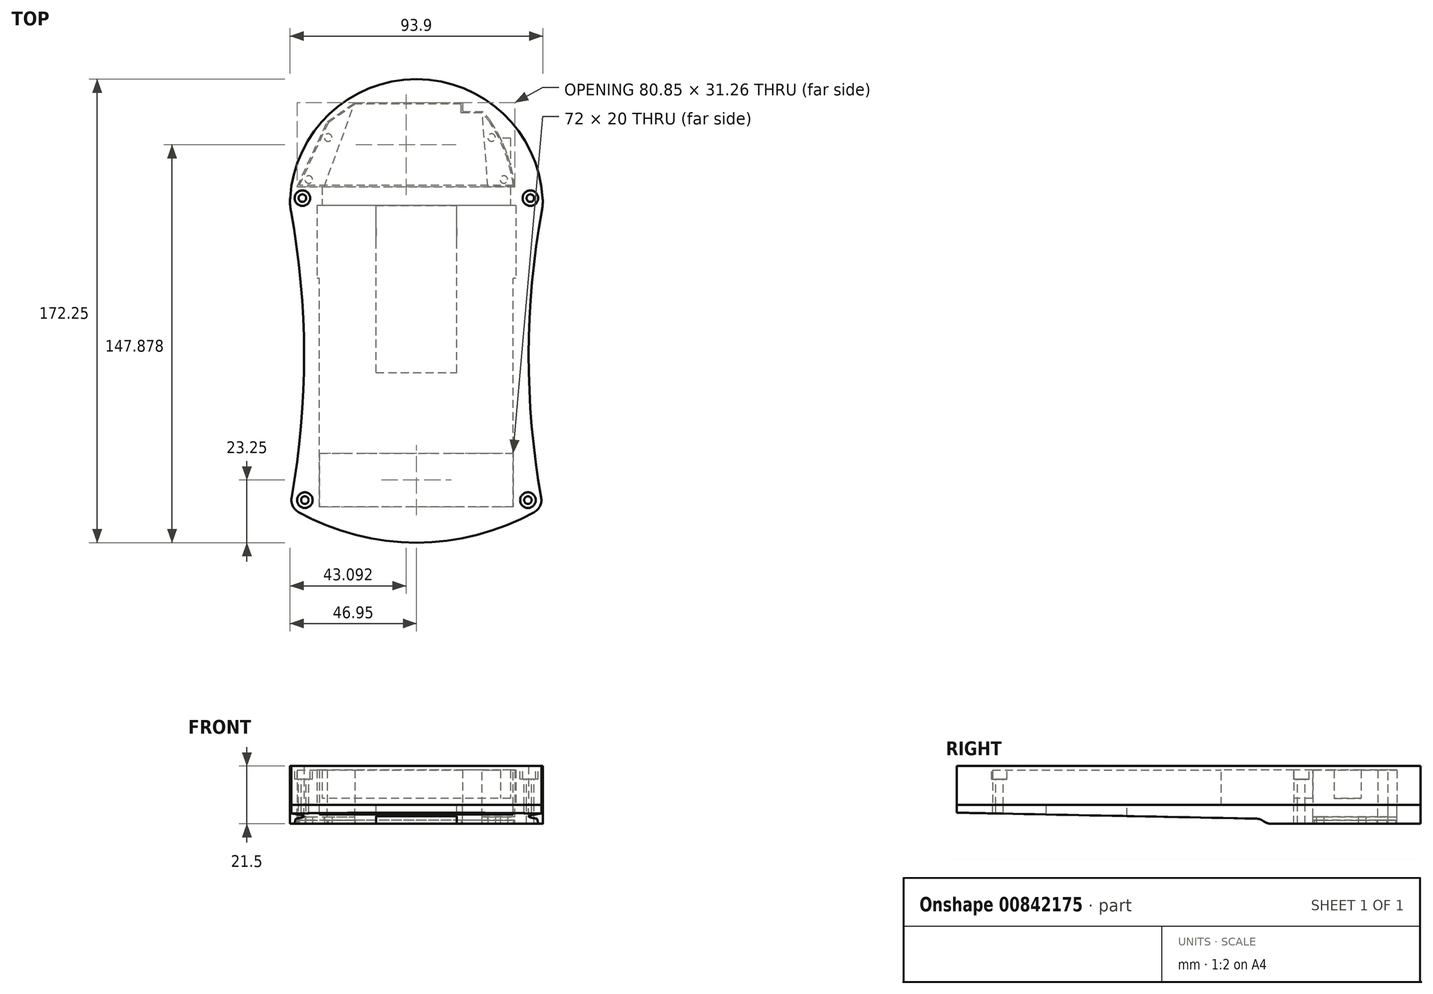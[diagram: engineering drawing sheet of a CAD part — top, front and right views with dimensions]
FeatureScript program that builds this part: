
annotation { "Feature Type Name" : "Feature", "Feature Type Description" : "" }
export const myFeature = defineFeature(function(context is Context, id is Id, definition is map)
    precondition{}
    {
        {
            var Q0;
            Q0=qCreatedBy(makeId("Top.planeOp"),FACE);
            var sketch = newSketch(context, id + "F0", { "sketchPlane" : qUnion([Q0])});
            skLineSegment(sketch, "E0.bottom", {"start": v(36, -56) * mm, "end": v(-36, -56) * mm});
            skLineSegment(sketch, "E0.top", {"start": v(36, 56) * mm, "end": v(-36, 56) * mm});
            skLineSegment(sketch, "E0.left", {"start": v(36, -56) * mm, "end": v(36, 56) * mm});
            skLineSegment(sketch, "E0.right", {"start": v(-36, -56) * mm, "end": v(-36, 56) * mm});
            skPoint(sketch, "E0.middle", {"position": v(0, 0) * mm});
            skArc(sketch, "E1", {"start": v(47, 56) * mm, "mid": v(0, 103) * mm, "end": v(-47, 56) * mm});
            skArc(sketch, "E2", {"start": v(-47, -56) * mm, "mid": v(-41.73, 0) * mm, "end": v(-47, 56) * mm});
            skLineSegment(sketch, "E3", {"start": v(0, 117.63) * mm, "end": v(0, -101.58) * mm, "construction": true});
            skLineSegment(sketch, "E4", {"start": v(-114.42, 0) * mm, "end": v(113.04, 0) * mm, "construction": true});
            skArc(sketch, "E5.MirrorCS", {"start": v(47, -56) * mm, "mid": v(0, -103) * mm, "end": v(-47, -56) * mm});
            skArc(sketch, "E6.MirrorCS", {"start": v(47, -56) * mm, "mid": v(41.73, 0) * mm, "end": v(47, 56) * mm});
            skSolve(sketch);
        }
        {
            var Q0;
            Q0=makeQuery(id+"F0.imprint","IMPRINT",FACE,{"disambiguationData":[TD([[makeQuery(id+"F0.imprint","IMPRINT",EDGE,{"derivedFrom":sQuery(id+"F0.wireOp",EDGE,"E0.bottom")}),1.0]])]});
            extrude(context, id + "F1", {"entities" : qUnion([Q0]), "depth" : 14.5 * mm, "offsetDistance" : 25 * mm});
        }
        {
            var Q0;
            Q0=makeQuery(id+"F1.opExtrude","CAP_FACE",FACE,{"disambiguationData":[OSD([sQuery(id+"F0.wireOp",EDGE,"E0.bottom"),sQuery(id+"F0.wireOp",EDGE,"E0.top"),sQuery(id+"F0.wireOp",EDGE,"E0.left"),sQuery(id+"F0.wireOp",EDGE,"E0.right"),sQuery(id+"F0.wireOp",EDGE,"E1"),sQuery(id+"F0.wireOp",EDGE,"E2"),sQuery(id+"F0.wireOp",EDGE,"E5.MirrorCS"),sQuery(id+"F0.wireOp",EDGE,"E6.MirrorCS")])],"isStart":false});
            var sketch = newSketch(context, id + "F2", { "sketchPlane" : qUnion([Q0])});
            skLineSegment(sketch, "E7.bottom", {"start": v(36, -56) * mm, "end": v(-36, -56) * mm});
            skLineSegment(sketch, "E7.top", {"start": v(36, 56) * mm, "end": v(-36, 56) * mm});
            skLineSegment(sketch, "E7.left", {"start": v(36, -56) * mm, "end": v(36, 56) * mm});
            skLineSegment(sketch, "E7.right", {"start": v(-36, -56) * mm, "end": v(-36, 56) * mm});
            skPoint(sketch, "E7.middle", {"position": v(0, 0) * mm});
            skSolve(sketch);
        }
        {
            var Q0;
            Q0=qSketchRegion(id+"F2",true);
            extrude(context, id + "F3", {"entities" : qUnion([Q0]), "operationType" : NewBodyOperationType.ADD, "oppositeDirection" : true, "depth" : 1.5 * mm, "offsetDistance" : 25 * mm});
        }
        {
            var Q0;
            Q0=makeQuery(id+"F1.opExtrude","CAP_FACE",FACE,{"disambiguationData":[OSD([sQuery(id+"F0.wireOp",EDGE,"E0.bottom"),sQuery(id+"F0.wireOp",EDGE,"E0.top"),sQuery(id+"F0.wireOp",EDGE,"E0.left"),sQuery(id+"F0.wireOp",EDGE,"E0.right"),sQuery(id+"F0.wireOp",EDGE,"E1"),sQuery(id+"F0.wireOp",EDGE,"E2"),sQuery(id+"F0.wireOp",EDGE,"E5.MirrorCS"),sQuery(id+"F0.wireOp",EDGE,"E6.MirrorCS")])],"isStart":true});
            var sketch = newSketch(context, id + "F4", { "sketchPlane" : qUnion([Q0])});
            skLineSegment(sketch, "E8", {"start": v(0, -56) * mm, "end": v(0, -29) * mm, "construction": true});
            skLineSegment(sketch, "E9.bottom", {"start": v(37, -56) * mm, "end": v(-37, -56) * mm});
            skLineSegment(sketch, "E9.top", {"start": v(37, -29) * mm, "end": v(-37, -29) * mm});
            skLineSegment(sketch, "E9.left", {"start": v(37, -56) * mm, "end": v(37, -29) * mm});
            skLineSegment(sketch, "E9.right", {"start": v(-37, -56) * mm, "end": v(-37, -29) * mm});
            skPoint(sketch, "E9.middle", {"position": v(0, -42.5) * mm});
            skSolve(sketch);
        }
        {
            var Q0;
            Q0=qSketchRegion(id+"F4",true);
            var Q1;
            Q1=makeQuery(id+"F3.opExtrude","CAP_FACE",FACE,{"disambiguationData":[OSD([sQuery(id+"F2.wireOp",EDGE,"E7.bottom"),sQuery(id+"F2.wireOp",EDGE,"E7.top"),sQuery(id+"F2.wireOp",EDGE,"E7.left"),sQuery(id+"F2.wireOp",EDGE,"E7.right")])],"isStart":false});
            extrude(context, id + "F5", {"entities" : qUnion([Q0]), "operationType" : NewBodyOperationType.REMOVE, "endBound" : BoundingType.UP_TO_SURFACE, "oppositeDirection" : true, "depth" : 25 * mm, "endBoundEntityFace" : qUnion([Q1]), "offsetDistance" : 25 * mm});
        }
        {
            var Q0;
            Q0=makeQuery(id+"F1.opExtrude","CAP_FACE",FACE,{"disambiguationData":[OSD([sQuery(id+"F0.wireOp",EDGE,"E0.bottom"),sQuery(id+"F0.wireOp",EDGE,"E0.top"),sQuery(id+"F0.wireOp",EDGE,"E0.left"),sQuery(id+"F0.wireOp",EDGE,"E0.right"),sQuery(id+"F0.wireOp",EDGE,"E1"),sQuery(id+"F0.wireOp",EDGE,"E2"),sQuery(id+"F0.wireOp",EDGE,"E5.MirrorCS"),sQuery(id+"F0.wireOp",EDGE,"E6.MirrorCS")])],"isStart":true});
            var sketch = newSketch(context, id + "F6", { "sketchPlane" : qUnion([Q0])});
            skArc(sketch, "E10", {"start": v(47, 56) * mm, "mid": v(0, 69.25) * mm, "end": v(-47, 56) * mm});
            skArc(sketch, "E11.0", {"start": v(47, 56) * mm, "mid": v(0, 103) * mm, "end": v(-47, 56) * mm});
            skSolve(sketch);
        }
        {
            var Q0;
            Q0=qSketchRegion(id+"F6",true);
            extrude(context, id + "F7", {"entities" : qUnion([Q0]), "operationType" : NewBodyOperationType.REMOVE, "oppositeDirection" : true, "depth" : 25 * mm, "offsetDistance" : 25 * mm});
        }
        {
            var Q0;
            Q0=makeQuery(id+"F1.opExtrude","CAP_FACE",FACE,{"disambiguationData":[OSD([sQuery(id+"F0.wireOp",EDGE,"E0.bottom"),sQuery(id+"F0.wireOp",EDGE,"E0.top"),sQuery(id+"F0.wireOp",EDGE,"E0.left"),sQuery(id+"F0.wireOp",EDGE,"E0.right"),sQuery(id+"F0.wireOp",EDGE,"E1"),sQuery(id+"F0.wireOp",EDGE,"E2"),sQuery(id+"F0.wireOp",EDGE,"E5.MirrorCS"),sQuery(id+"F0.wireOp",EDGE,"E6.MirrorCS")])],"isStart":true});
            var sketch = newSketch(context, id + "F8", { "sketchPlane" : qUnion([Q0])});
            skArc(sketch, "E12", {"start": v(27.76, -87.12) * mm, "mid": v(33.54, -75.56) * mm, "end": v(36.57, -63) * mm});
            skLineSegment(sketch, "E13", {"start": v(0, 109.51) * mm, "end": v(0, -146.95) * mm, "construction": true});
            skArc(sketch, "E14.MirrorCS", {"start": v(-27.76, -87.12) * mm, "mid": v(-33.54, -75.56) * mm, "end": v(-36.57, -63) * mm});
            skLineSegment(sketch, "E15", {"start": v(-36.57, -63) * mm, "end": v(36.57, -63) * mm});
            skPoint(sketch, "E16.orphan", {"position": v(-47, -56) * mm});
            skPoint(sketch, "E17.orphan", {"position": v(47, -56) * mm});
            skPoint(sketch, "E18.orphan", {"position": v(37, -56) * mm});
            skPoint(sketch, "E19.orphan", {"position": v(-37, -56) * mm});
            skArc(sketch, "E20.0", {"start": v(20.57, -93.76) * mm, "mid": v(0, -99) * mm, "end": v(-20.57, -93.76) * mm});
            skPoint(sketch, "E21.orphan", {"position": v(-16, -100.2) * mm});
            skPoint(sketch, "E22.orphan", {"position": v(16, -100.2) * mm});
            skPoint(sketch, "E23.visualSharp", {"position": v(-25, -90.99) * mm});
            skArc(sketch, "E23.filletArc", {"start": v(-27.76, -87.12) * mm, "mid": v(-24.57, -90.89) * mm, "end": v(-20.57, -93.76) * mm});
            skPoint(sketch, "E24.visualSharp", {"position": v(25, -90.99) * mm});
            skArc(sketch, "E24.filletArc", {"start": v(20.57, -93.76) * mm, "mid": v(24.57, -90.89) * mm, "end": v(27.76, -87.12) * mm});
            skSolve(sketch);
        }
        {
            var Q0;
            Q0=qSketchRegion(id+"F8",true);
            extrude(context, id + "F9", {"entities" : qUnion([Q0]), "operationType" : NewBodyOperationType.REMOVE, "oppositeDirection" : true, "depth" : 13 * mm, "offsetDistance" : 25 * mm});
        }
        {
            var Q0;
            Q0=makeQuery(id+"F1.opExtrude","SWEPT_EDGE",EDGE,{"disambiguationData":[OSD([sQuery(id+"F0.wireOp",EDGE,"E1"),sQuery(id+"F0.wireOp",EDGE,"E2")])]});
            var Q1;
            Q1=makeQuery(id+"F1.opExtrude","SWEPT_EDGE",EDGE,{"disambiguationData":[OSD([sQuery(id+"F0.wireOp",EDGE,"E1"),sQuery(id+"F0.wireOp",EDGE,"E6.MirrorCS")])]});
            fillet(context, id + "F10", {"entities" : qUnion([Q0, Q1]), "radius" : 20 * mm, "tangentPropagation" : true, "allowEdgeOverflow" : false});
        }
        {
            var Q0;
            {var subQ0=sQuery(id+"F0.wireOp",EDGE,"E6.MirrorCS");Q0=makeQuery(id+"F7.boolean.opBoolean","MERGE",EDGE,{"derivedFrom":[makeQuery(id+"F1.opExtrude","SWEPT_EDGE",EDGE,{"disambiguationData":[OSD([sQuery(id+"F0.wireOp",EDGE,"E5.MirrorCS"),subQ0])]}),makeQuery(id+"F7.opExtrude","SWEPT_EDGE",EDGE,{"disambiguationData":[OSD([subQ0,sQuery(id+"F6.wireOp",EDGE,"E10"),sQuery(id+"F6.wireOp",EDGE,"E11.0")])]})]});}
            var Q1;
            {var subQ0=sQuery(id+"F0.wireOp",EDGE,"E2");Q1=makeQuery(id+"F7.boolean.opBoolean","MERGE",EDGE,{"derivedFrom":[makeQuery(id+"F1.opExtrude","SWEPT_EDGE",EDGE,{"disambiguationData":[OSD([subQ0,sQuery(id+"F0.wireOp",EDGE,"E5.MirrorCS")])]}),makeQuery(id+"F7.opExtrude","SWEPT_EDGE",EDGE,{"disambiguationData":[OSD([subQ0,sQuery(id+"F6.wireOp",EDGE,"E10"),sQuery(id+"F6.wireOp",EDGE,"E11.0")])]})]});}
            fillet(context, id + "F11", {"entities" : qUnion([Q0, Q1]), "radius" : 5 * mm, "tangentPropagation" : true, "allowEdgeOverflow" : false});
        }
        {
            var Q0;
            Q0=makeQuery(id+"F3.boolean.opBoolean","MERGE",FACE,{"derivedFrom":[makeQuery(id+"F1.opExtrude","CAP_FACE",FACE,{"disambiguationData":[OSD([sQuery(id+"F0.wireOp",EDGE,"E0.bottom"),sQuery(id+"F0.wireOp",EDGE,"E0.top"),sQuery(id+"F0.wireOp",EDGE,"E0.left"),sQuery(id+"F0.wireOp",EDGE,"E0.right"),sQuery(id+"F0.wireOp",EDGE,"E1"),sQuery(id+"F0.wireOp",EDGE,"E2"),sQuery(id+"F0.wireOp",EDGE,"E5.MirrorCS"),sQuery(id+"F0.wireOp",EDGE,"E6.MirrorCS")])],"isStart":false}),makeQuery(id+"F3.opExtrude","CAP_FACE",FACE,{"disambiguationData":[OSD([sQuery(id+"F2.wireOp",EDGE,"E7.bottom"),sQuery(id+"F2.wireOp",EDGE,"E7.top"),sQuery(id+"F2.wireOp",EDGE,"E7.left"),sQuery(id+"F2.wireOp",EDGE,"E7.right")])],"isStart":true})]});
            var sketch = newSketch(context, id + "F12", { "sketchPlane" : qUnion([Q0])});
            skCircle(sketch, "E25", {"center": v(-42.35, 58.78) * mm, "radius": 2.9 * mm});
            skLineSegment(sketch, "E26", {"start": v(0, 101.03) * mm, "end": v(0, -86.28) * mm, "construction": true});
            skCircle(sketch, "E27.MirrorC", {"center": v(42.35, 58.78) * mm, "radius": 2.9 * mm});
            skCircle(sketch, "E28", {"center": v(-41.45, -53.46) * mm, "radius": 2.9 * mm});
            skCircle(sketch, "E29.MirrorC", {"center": v(41.45, -53.46) * mm, "radius": 2.9 * mm});
            skSolve(sketch);
        }
        {
            var Q0;
            Q0=qSketchRegion(id+"F12",true);
            extrude(context, id + "F13", {"entities" : qUnion([Q0]), "operationType" : NewBodyOperationType.REMOVE, "oppositeDirection" : true, "depth" : 5 * mm, "offsetDistance" : 25 * mm});
        }
        {
            var Q0;
            Q0=makeQuery(id+"F13.boolean.opBoolean","COPY",FACE,{"derivedFrom":makeQuery(id+"F13.opExtrude","CAP_FACE",FACE,{"disambiguationData":[OSD([sQuery(id+"F12.wireOp",EDGE,"E25")])],"isStart":false})});
            var sketch = newSketch(context, id + "F14", { "sketchPlane" : qUnion([Q0])});
            skCircle(sketch, "E30", {"center": v(-42.35, 58.78) * mm, "radius": 1.4 * mm});
            skLineSegment(sketch, "E31", {"start": v(0, 85.8) * mm, "end": v(0, -75.06) * mm, "construction": true});
            skCircle(sketch, "E32", {"center": v(-41.45, -53.46) * mm, "radius": 1.4 * mm});
            skCircle(sketch, "E33.MirrorC", {"center": v(42.35, 58.78) * mm, "radius": 1.4 * mm});
            skCircle(sketch, "E34.MirrorC", {"center": v(41.45, -53.46) * mm, "radius": 1.4 * mm});
            skSolve(sketch);
        }
        {
            var Q0;
            Q0=qSketchRegion(id+"F14",true);
            extrude(context, id + "F15", {"entities" : qUnion([Q0]), "operationType" : NewBodyOperationType.REMOVE, "oppositeDirection" : true, "depth" : 25 * mm, "offsetDistance" : 25 * mm});
        }
        {
            var Q0;
            Q0=makeQuery(id+"F5.boolean.opBoolean","MERGE",FACE,{"derivedFrom":[makeQuery(id+"F1.opExtrude","SWEPT_FACE",FACE,{"disambiguationData":[OSD([sQuery(id+"F0.wireOp",EDGE,"E0.top")])]}),makeQuery(id+"F5.opExtrude","SWEPT_FACE",FACE,{"disambiguationData":[OSD([sQuery(id+"F4.wireOp",EDGE,"E9.bottom")])]})]});
            var sketch = newSketch(context, id + "F16", { "sketchPlane" : qUnion([Q0])});
            skLineSegment(sketch, "E35.bottom", {"start": v(-35, 13) * mm, "end": v(35, 13) * mm});
            skLineSegment(sketch, "E35.left", {"start": v(-35, 13) * mm, "end": v(-35, 2.5) * mm});
            skLineSegment(sketch, "E35.right", {"start": v(35, 13) * mm, "end": v(35, 2.5) * mm});
            skPoint(sketch, "E35.middle", {"position": v(0, 6.5) * mm});
            skLineSegment(sketch, "E36", {"start": v(35, 2.5) * mm, "end": v(-35, 2.5) * mm});
            skPoint(sketch, "E37.orphan", {"position": v(35, 0) * mm});
            skPoint(sketch, "E38.orphan", {"position": v(-35, 0) * mm});
            skSolve(sketch);
        }
        {
            var Q0;
            Q0=qSketchRegion(id+"F16",true);
            extrude(context, id + "F17", {"entities" : qUnion([Q0]), "operationType" : NewBodyOperationType.REMOVE, "oppositeDirection" : true, "depth" : 25 * mm, "offsetDistance" : 25 * mm});
        }
        {
            var Q0;
            Q0=makeQuery(id+"F9.boolean.opBoolean","COPY",FACE,{"derivedFrom":makeQuery(id+"F9.opExtrude","CAP_FACE",FACE,{"disambiguationData":[OSD([sQuery(id+"F8.wireOp",EDGE,"E12"),sQuery(id+"F8.wireOp",EDGE,"E14.MirrorCS"),sQuery(id+"F8.wireOp",EDGE,"E15"),sQuery(id+"F8.wireOp",EDGE,"E20.0"),sQuery(id+"F8.wireOp",EDGE,"E23.filletArc"),sQuery(id+"F8.wireOp",EDGE,"E24.filletArc")])],"isStart":false})});
            var sketch = newSketch(context, id + "F18", { "sketchPlane" : qUnion([Q0])});
            skPoint(sketch, "E39", {"position": v(24.45, -91) * mm});
            skLineSegment(sketch, "E40", {"start": v(24.45, -91) * mm, "end": v(-24.45, -91) * mm});
            skArc(sketch, "E41.0", {"start": v(-24.45, -91) * mm, "mid": v(-22.6, -92.5) * mm, "end": v(-20.57, -93.76) * mm});
            skArc(sketch, "E42.0", {"start": v(20.57, -93.76) * mm, "mid": v(0, -99) * mm, "end": v(-20.57, -93.76) * mm});
            skArc(sketch, "E43.0", {"start": v(20.57, -93.76) * mm, "mid": v(22.6, -92.5) * mm, "end": v(24.45, -91) * mm});
            skPoint(sketch, "E44.orphan", {"position": v(-27.76, -87.12) * mm});
            skPoint(sketch, "E45.orphan", {"position": v(27.76, -87.12) * mm});
            skSolve(sketch);
        }
        {
            var Q0;
            Q0=qSketchRegion(id+"F18",true);
            var Q1;
            Q1=makeQuery(id+"F1.opExtrude","CAP_FACE",FACE,{"disambiguationData":[OSD([sQuery(id+"F0.wireOp",EDGE,"E0.bottom"),sQuery(id+"F0.wireOp",EDGE,"E0.top"),sQuery(id+"F0.wireOp",EDGE,"E0.left"),sQuery(id+"F0.wireOp",EDGE,"E0.right"),sQuery(id+"F0.wireOp",EDGE,"E1"),sQuery(id+"F0.wireOp",EDGE,"E2"),sQuery(id+"F0.wireOp",EDGE,"E5.MirrorCS"),sQuery(id+"F0.wireOp",EDGE,"E6.MirrorCS")])],"isStart":true});
            extrude(context, id + "F19", {"entities" : qUnion([Q0]), "operationType" : NewBodyOperationType.ADD, "endBound" : BoundingType.UP_TO_SURFACE, "depth" : 25 * mm, "endBoundEntityFace" : qUnion([Q1]), "offsetDistance" : 25 * mm});
        }
        {
            var Q0;
            {var subQ0=sQuery(id+"F0.wireOp",EDGE,"E6.MirrorCS");var subQ1=sQuery(id+"F0.wireOp",EDGE,"E5.MirrorCS");var subQ2=sQuery(id+"F0.wireOp",EDGE,"E2");var subQ3=sQuery(id+"F0.wireOp",EDGE,"E1");var subQ4=sQuery(id+"F0.wireOp",EDGE,"E0.right");var subQ5=sQuery(id+"F0.wireOp",EDGE,"E0.left");var subQ6=sQuery(id+"F0.wireOp",EDGE,"E0.top");var subQ7=sQuery(id+"F0.wireOp",EDGE,"E0.bottom");Q0=makeQuery(id+"F19.boolean.opBoolean","MERGE",FACE,{"derivedFrom":[makeQuery(id+"F1.opExtrude","CAP_FACE",FACE,{"disambiguationData":[OSD([subQ7,subQ6,subQ5,subQ4,subQ3,subQ2,subQ1,subQ0])],"isStart":true}),makeQuery(id+"F19.opExtrude","CAP_FACE",FACE,{"disambiguationData":[OSD([subQ7,subQ6,subQ5,subQ4,subQ3,subQ2,subQ1,subQ0])],"isStart":false})]});}
            var sketch = newSketch(context, id + "F20", { "sketchPlane" : qUnion([Q0])});
            skLineSegment(sketch, "E46", {"start": v(-40.9, -63) * mm, "end": v(-33.2, -87.12) * mm});
            skLineSegment(sketch, "E47", {"start": v(-22.9, -63) * mm, "end": v(-40.9, -63) * mm});
            skLineSegment(sketch, "E48", {"start": v(-33.2, -87.12) * mm, "end": v(-22.9, -94.26) * mm});
            skLineSegment(sketch, "E49", {"start": v(-22.9, -94.26) * mm, "end": v(17.1, -94.26) * mm});
            skLineSegment(sketch, "E50", {"start": v(17.1, -94.26) * mm, "end": v(17.1, -63) * mm});
            skLineSegment(sketch, "E51", {"start": v(17.1, -63) * mm, "end": v(-22.9, -63) * mm});
            skSolve(sketch);
        }
        {
            var Q0;
            Q0=qSketchRegion(id+"F20",true);
            var Q1;
            {var subQ0=sQuery(id+"F2.wireOp",EDGE,"E7.right");var subQ1=sQuery(id+"F2.wireOp",EDGE,"E7.left");var subQ2=sQuery(id+"F2.wireOp",EDGE,"E7.top");var subQ3=sQuery(id+"F2.wireOp",EDGE,"E7.bottom");Q1=makeQuery(id+"F17.boolean.opBoolean","MERGE",FACE,{"derivedFrom":[makeQuery(id+"F5.boolean.opBoolean","MERGE",FACE,{"derivedFrom":[makeQuery(id+"F3.opExtrude","CAP_FACE",FACE,{"disambiguationData":[OSD([subQ3,subQ2,subQ1,subQ0])],"isStart":false}),makeQuery(id+"F5.opExtrude","CAP_FACE",FACE,{"disambiguationData":[OSD([subQ3,subQ2,subQ1,subQ0])],"isStart":false})]}),makeQuery(id+"F9.boolean.opBoolean","COPY",FACE,{"derivedFrom":makeQuery(id+"F9.opExtrude","CAP_FACE",FACE,{"disambiguationData":[OSD([sQuery(id+"F8.wireOp",EDGE,"E12"),sQuery(id+"F8.wireOp",EDGE,"E14.MirrorCS"),sQuery(id+"F8.wireOp",EDGE,"E15"),sQuery(id+"F8.wireOp",EDGE,"E20.0"),sQuery(id+"F8.wireOp",EDGE,"E23.filletArc"),sQuery(id+"F8.wireOp",EDGE,"E24.filletArc")])],"isStart":false})}),makeQuery(id+"F17.opExtrude","SWEPT_FACE",FACE,{"disambiguationData":[OSD([sQuery(id+"F16.wireOp",EDGE,"E35.bottom")])]})]});}
            extrude(context, id + "F21", {"entities" : qUnion([Q0]), "operationType" : NewBodyOperationType.REMOVE, "endBound" : BoundingType.UP_TO_SURFACE, "oppositeDirection" : true, "depth" : 25 * mm, "endBoundEntityFace" : qUnion([Q1]), "offsetDistance" : 25 * mm});
        }
        {
            var Q0;
            {var subQ0=sQuery(id+"F0.wireOp",EDGE,"E6.MirrorCS");var subQ1=sQuery(id+"F0.wireOp",EDGE,"E5.MirrorCS");var subQ2=sQuery(id+"F0.wireOp",EDGE,"E2");var subQ3=sQuery(id+"F0.wireOp",EDGE,"E1");var subQ4=sQuery(id+"F0.wireOp",EDGE,"E0.right");var subQ5=sQuery(id+"F0.wireOp",EDGE,"E0.left");var subQ6=sQuery(id+"F0.wireOp",EDGE,"E0.top");var subQ7=sQuery(id+"F0.wireOp",EDGE,"E0.bottom");Q0=makeQuery(id+"F19.boolean.opBoolean","MERGE",FACE,{"derivedFrom":[makeQuery(id+"F1.opExtrude","CAP_FACE",FACE,{"disambiguationData":[OSD([subQ7,subQ6,subQ5,subQ4,subQ3,subQ2,subQ1,subQ0])],"isStart":true}),makeQuery(id+"F19.opExtrude","CAP_FACE",FACE,{"disambiguationData":[OSD([subQ7,subQ6,subQ5,subQ4,subQ3,subQ2,subQ1,subQ0])],"isStart":false})]});}
            var sketch = newSketch(context, id + "F22", { "sketchPlane" : qUnion([Q0])});
            skLineSegment(sketch, "E52", {"start": v(-40.9, -63) * mm, "end": v(-44.28, -63) * mm});
            skLineSegment(sketch, "E53", {"start": v(-44.28, -63) * mm, "end": v(-33.2, -87.12) * mm});
            skLineSegment(sketch, "E54.0", {"start": v(-40.9, -63) * mm, "end": v(-33.2, -87.12) * mm});
            skSolve(sketch);
        }
        {
            var Q0;
            Q0=qSketchRegion(id+"F22",true);
            var Q1;
            {var subQ0=sQuery(id+"F16.wireOp",EDGE,"E35.bottom");var subQ1=sQuery(id+"F8.wireOp",EDGE,"E24.filletArc");var subQ2=sQuery(id+"F8.wireOp",EDGE,"E23.filletArc");var subQ3=sQuery(id+"F8.wireOp",EDGE,"E20.0");var subQ4=sQuery(id+"F8.wireOp",EDGE,"E15");var subQ5=sQuery(id+"F8.wireOp",EDGE,"E14.MirrorCS");var subQ6=sQuery(id+"F8.wireOp",EDGE,"E12");var subQ7=sQuery(id+"F2.wireOp",EDGE,"E7.right");var subQ8=sQuery(id+"F2.wireOp",EDGE,"E7.left");var subQ9=sQuery(id+"F2.wireOp",EDGE,"E7.top");var subQ10=sQuery(id+"F2.wireOp",EDGE,"E7.bottom");Q1=makeQuery(id+"F21.boolean.opBoolean","MERGE",FACE,{"derivedFrom":[makeQuery(id+"F17.boolean.opBoolean","MERGE",FACE,{"derivedFrom":[makeQuery(id+"F5.boolean.opBoolean","MERGE",FACE,{"derivedFrom":[makeQuery(id+"F3.opExtrude","CAP_FACE",FACE,{"disambiguationData":[OSD([subQ10,subQ9,subQ8,subQ7])],"isStart":false}),makeQuery(id+"F5.opExtrude","CAP_FACE",FACE,{"disambiguationData":[OSD([subQ10,subQ9,subQ8,subQ7])],"isStart":false})]}),makeQuery(id+"F9.boolean.opBoolean","COPY",FACE,{"derivedFrom":makeQuery(id+"F9.opExtrude","CAP_FACE",FACE,{"disambiguationData":[OSD([subQ6,subQ5,subQ4,subQ3,subQ2,subQ1])],"isStart":false})}),makeQuery(id+"F17.opExtrude","SWEPT_FACE",FACE,{"disambiguationData":[OSD([subQ0])]})]}),makeQuery(id+"F21.opExtrude","CAP_FACE",FACE,{"disambiguationData":[OSD([subQ10,subQ9,subQ8,subQ7,subQ6,subQ5,subQ4,subQ3,subQ2,subQ1,subQ0])],"isStart":false})]});}
            extrude(context, id + "F23", {"entities" : qUnion([Q0]), "operationType" : NewBodyOperationType.REMOVE, "endBound" : BoundingType.UP_TO_SURFACE, "oppositeDirection" : true, "depth" : 25 * mm, "endBoundEntityFace" : qUnion([Q1]), "offsetDistance" : 25 * mm});
        }
        {
            var Q0;
            {var subQ0=sQuery(id+"F0.wireOp",EDGE,"E6.MirrorCS");var subQ1=sQuery(id+"F0.wireOp",EDGE,"E5.MirrorCS");var subQ2=sQuery(id+"F0.wireOp",EDGE,"E2");var subQ3=sQuery(id+"F0.wireOp",EDGE,"E1");var subQ4=sQuery(id+"F0.wireOp",EDGE,"E0.right");var subQ5=sQuery(id+"F0.wireOp",EDGE,"E0.left");var subQ6=sQuery(id+"F0.wireOp",EDGE,"E0.top");var subQ7=sQuery(id+"F0.wireOp",EDGE,"E0.bottom");Q0=makeQuery(id+"F19.boolean.opBoolean","MERGE",FACE,{"derivedFrom":[makeQuery(id+"F1.opExtrude","CAP_FACE",FACE,{"disambiguationData":[OSD([subQ7,subQ6,subQ5,subQ4,subQ3,subQ2,subQ1,subQ0])],"isStart":true}),makeQuery(id+"F19.opExtrude","CAP_FACE",FACE,{"disambiguationData":[OSD([subQ7,subQ6,subQ5,subQ4,subQ3,subQ2,subQ1,subQ0])],"isStart":false})]});}
            var sketch = newSketch(context, id + "F24", { "sketchPlane" : qUnion([Q0])});
            skArc(sketch, "E55.0", {"start": v(46.92, -58.78) * mm, "mid": v(0, -103) * mm, "end": v(-46.92, -58.78) * mm});
            skArc(sketch, "E55.1", {"start": v(46.37, 52.58) * mm, "mid": v(45.97, 55.6) * mm, "end": v(43.89, 57.82) * mm});
            skArc(sketch, "E55.2", {"start": v(43.89, 57.82) * mm, "mid": v(0, 69.25) * mm, "end": v(-43.89, 57.82) * mm});
            skArc(sketch, "E55.3", {"start": v(-46.37, 52.58) * mm, "mid": v(-41.73, -0.72) * mm, "end": v(-46.63, -54) * mm});
            skArc(sketch, "E55.4", {"start": v(46.37, 52.58) * mm, "mid": v(41.73, -0.72) * mm, "end": v(46.63, -54) * mm});
            skLineSegment(sketch, "E55.5", {"start": v(-33.2, -87.12) * mm, "end": v(-22.9, -94.26) * mm});
            skArc(sketch, "E56.0", {"start": v(-43.89, 57.82) * mm, "mid": v(-45.97, 55.6) * mm, "end": v(-46.37, 52.58) * mm});
            skCircle(sketch, "E57.0", {"center": v(41.45, 53.46) * mm, "radius": 1.4 * mm});
            skArc(sketch, "E58.0", {"start": v(46.92, -58.78) * mm, "mid": v(46.92, -56.38) * mm, "end": v(46.63, -54) * mm});
            skArc(sketch, "E59.0", {"start": v(-46.63, -54) * mm, "mid": v(-46.92, -56.38) * mm, "end": v(-46.92, -58.78) * mm});
            skCircle(sketch, "E60.0", {"center": v(-42.35, -58.78) * mm, "radius": 1.4 * mm});
            skCircle(sketch, "E61.0", {"center": v(42.35, -58.78) * mm, "radius": 1.4 * mm});
            skCircle(sketch, "E62.0", {"center": v(-41.45, 53.46) * mm, "radius": 1.4 * mm});
            skLineSegment(sketch, "E63.0", {"start": v(-22.9, -94.26) * mm, "end": v(17.1, -94.26) * mm});
            skLineSegment(sketch, "E64.0", {"start": v(17.1, -94.26) * mm, "end": v(17.1, -91) * mm});
            skLineSegment(sketch, "E65.0", {"start": v(17.1, -91) * mm, "end": v(24.45, -91) * mm});
            skArc(sketch, "E66.0", {"start": v(24.45, -91) * mm, "mid": v(26.23, -89.16) * mm, "end": v(27.76, -87.12) * mm});
            skArc(sketch, "E67.0", {"start": v(27.76, -87.12) * mm, "mid": v(33.54, -75.56) * mm, "end": v(36.57, -63) * mm});
            skLineSegment(sketch, "E68.0", {"start": v(-44.28, -63) * mm, "end": v(36.57, -63) * mm});
            skLineSegment(sketch, "E69.0", {"start": v(-44.28, -63) * mm, "end": v(-33.2, -87.12) * mm});
            skSolve(sketch);
        }
        {
            var Q0;
            Q0=qSketchRegion(id+"F24",true);
            extrude(context, id + "F25", {"entities" : qUnion([Q0]), "depth" : 7 * mm, "offsetDistance" : 25 * mm});
        }
        {
            var Q0;
            Q0=qCreatedBy(makeId("Right.planeOp"),FACE);
            var sketch = newSketch(context, id + "F26", { "sketchPlane" : qUnion([Q0])});
            skLineSegment(sketch, "E70", {"start": v(-69.25, -2.86) * mm, "end": v(45.75, -5.15) * mm});
            skLineSegment(sketch, "E71", {"start": v(45.75, -5.15) * mm, "end": v(45.75, -7) * mm});
            skLineSegment(sketch, "E72", {"start": v(-69.25, -2.86) * mm, "end": v(-69.25, -7) * mm});
            skLineSegment(sketch, "E73", {"start": v(-69.25, -7) * mm, "end": v(45.75, -7) * mm});
            skSolve(sketch);
        }
        {
            var Q0;
            Q0=qSketchRegion(id+"F26",true);
            extrude(context, id + "F27", {"entities" : qUnion([Q0]), "operationType" : NewBodyOperationType.REMOVE, "endBound" : BoundingType.SYMMETRIC, "oppositeDirection" : true, "depth" : 147.6 * mm, "offsetDistance" : 25 * mm});
        }
        {
            var Q0;
            Q0=makeQuery(id+"F27.boolean.opBoolean","COPY",EDGE,{"derivedFrom":makeQuery(id+"F27.opExtrude","SWEPT_EDGE",EDGE,{"disambiguationData":[OSD([sQuery(id+"F26.wireOp",EDGE,"E70"),sQuery(id+"F26.wireOp",EDGE,"E71")])]})});
            fillet(context, id + "F28", {"entities" : qUnion([Q0]), "radius" : 5 * mm, "tangentPropagation" : true, "allowEdgeOverflow" : false});
        }
        {
            var Q0;
            Q0=makeQuery(id+"F28.opFillet","BLEND_EDGE",EDGE,{"blendedFrom":[makeQuery(id+"F27.boolean.opBoolean","COPY",EDGE,{"derivedFrom":makeQuery(id+"F27.opExtrude","SWEPT_EDGE",EDGE,{"disambiguationData":[OSD([sQuery(id+"F26.wireOp",EDGE,"E70"),sQuery(id+"F26.wireOp",EDGE,"E71")])]})}),makeQuery(id+"F25.opExtrude","CAP_FACE",FACE,{"disambiguationData":[OSD([sQuery(id+"F24.wireOp",EDGE,"E55.0"),sQuery(id+"F24.wireOp",EDGE,"E55.1"),sQuery(id+"F24.wireOp",EDGE,"E55.2"),sQuery(id+"F24.wireOp",EDGE,"E55.3"),sQuery(id+"F24.wireOp",EDGE,"E55.4"),sQuery(id+"F24.wireOp",EDGE,"E55.5"),sQuery(id+"F24.wireOp",EDGE,"E56.0"),sQuery(id+"F24.wireOp",EDGE,"E57.0"),sQuery(id+"F24.wireOp",EDGE,"E58.0"),sQuery(id+"F24.wireOp",EDGE,"E59.0"),sQuery(id+"F24.wireOp",EDGE,"E60.0"),sQuery(id+"F24.wireOp",EDGE,"E61.0"),sQuery(id+"F24.wireOp",EDGE,"E62.0"),sQuery(id+"F24.wireOp",EDGE,"E63.0"),sQuery(id+"F24.wireOp",EDGE,"E64.0"),sQuery(id+"F24.wireOp",EDGE,"E65.0"),sQuery(id+"F24.wireOp",EDGE,"E66.0"),sQuery(id+"F24.wireOp",EDGE,"E67.0"),sQuery(id+"F24.wireOp",EDGE,"E68.0"),sQuery(id+"F24.wireOp",EDGE,"E69.0")])],"isStart":false})],"blendedInto":[makeQuery(id+"F25.opExtrude","CAP_FACE",FACE,{"disambiguationData":[OSD([sQuery(id+"F24.wireOp",EDGE,"E55.0"),sQuery(id+"F24.wireOp",EDGE,"E55.1"),sQuery(id+"F24.wireOp",EDGE,"E55.2"),sQuery(id+"F24.wireOp",EDGE,"E55.3"),sQuery(id+"F24.wireOp",EDGE,"E55.4"),sQuery(id+"F24.wireOp",EDGE,"E55.5"),sQuery(id+"F24.wireOp",EDGE,"E56.0"),sQuery(id+"F24.wireOp",EDGE,"E57.0"),sQuery(id+"F24.wireOp",EDGE,"E58.0"),sQuery(id+"F24.wireOp",EDGE,"E59.0"),sQuery(id+"F24.wireOp",EDGE,"E60.0"),sQuery(id+"F24.wireOp",EDGE,"E61.0"),sQuery(id+"F24.wireOp",EDGE,"E62.0"),sQuery(id+"F24.wireOp",EDGE,"E63.0"),sQuery(id+"F24.wireOp",EDGE,"E64.0"),sQuery(id+"F24.wireOp",EDGE,"E65.0"),sQuery(id+"F24.wireOp",EDGE,"E66.0"),sQuery(id+"F24.wireOp",EDGE,"E67.0"),sQuery(id+"F24.wireOp",EDGE,"E68.0"),sQuery(id+"F24.wireOp",EDGE,"E69.0")])],"isStart":false})]});
            fillet(context, id + "F29", {"entities" : qUnion([Q0]), "radius" : 5 * mm, "tangentPropagation" : true, "allowEdgeOverflow" : false});
        }
        {
            var Q0;
            Q0=makeQuery(id+"F25.opExtrude","CAP_FACE",FACE,{"disambiguationData":[OSD([sQuery(id+"F24.wireOp",EDGE,"E55.0"),sQuery(id+"F24.wireOp",EDGE,"E55.1"),sQuery(id+"F24.wireOp",EDGE,"E55.2"),sQuery(id+"F24.wireOp",EDGE,"E55.3"),sQuery(id+"F24.wireOp",EDGE,"E55.4"),sQuery(id+"F24.wireOp",EDGE,"E55.5"),sQuery(id+"F24.wireOp",EDGE,"E56.0"),sQuery(id+"F24.wireOp",EDGE,"E57.0"),sQuery(id+"F24.wireOp",EDGE,"E58.0"),sQuery(id+"F24.wireOp",EDGE,"E59.0"),sQuery(id+"F24.wireOp",EDGE,"E60.0"),sQuery(id+"F24.wireOp",EDGE,"E61.0"),sQuery(id+"F24.wireOp",EDGE,"E62.0"),sQuery(id+"F24.wireOp",EDGE,"E63.0"),sQuery(id+"F24.wireOp",EDGE,"E64.0"),sQuery(id+"F24.wireOp",EDGE,"E65.0"),sQuery(id+"F24.wireOp",EDGE,"E66.0"),sQuery(id+"F24.wireOp",EDGE,"E67.0"),sQuery(id+"F24.wireOp",EDGE,"E68.0"),sQuery(id+"F24.wireOp",EDGE,"E69.0")])],"isStart":false});
            cPlane(context, id + "F30", {"entities" : qUnion([Q0]), "cplaneType" : CPlaneType.OFFSET, "offset" : 2.6 * mm, "oppositeDirection" : true, "width" : 150 * mm, "height" : 150 * mm});
        }
        {
            var Q0;
            Q0=qCreatedBy(id+"F30.planeOp",FACE);
            var sketch = newSketch(context, id + "F31", { "sketchPlane" : qUnion([Q0])});
            skLineSegment(sketch, "E74.0", {"start": v(-44.28, -63) * mm, "end": v(-34.28, -84.76) * mm});
            skLineSegment(sketch, "E75", {"start": v(-44.28, -63) * mm, "end": v(-34.28, -63) * mm});
            skPoint(sketch, "E76.orphan", {"position": v(-33.2, -87.12) * mm});
            skLineSegment(sketch, "E77", {"start": v(0, 7.8) * mm, "end": v(0, -94.03) * mm, "construction": true});
            skArc(sketch, "E78.0", {"start": v(27.76, -87.12) * mm, "mid": v(33.54, -75.56) * mm, "end": v(36.57, -63) * mm});
            skLineSegment(sketch, "E79", {"start": v(36.57, -63) * mm, "end": v(26.57, -63) * mm});
            skArc(sketch, "E80.0", {"start": v(26.57, -88.75) * mm, "mid": v(27.18, -87.95) * mm, "end": v(27.76, -87.12) * mm});
            skPoint(sketch, "E81.orphan", {"position": v(24.45, -91) * mm});
            skLineSegment(sketch, "E82.0", {"start": v(-44.28, -63) * mm, "end": v(-33.2, -87.12) * mm});
            skLineSegment(sketch, "E83.0", {"start": v(-33.2, -87.12) * mm, "end": v(-22.9, -94.26) * mm});
            skArc(sketch, "E84.0", {"start": v(24.45, -91) * mm, "mid": v(26.23, -89.16) * mm, "end": v(27.76, -87.12) * mm});
            skLineSegment(sketch, "E85", {"start": v(-34.28, -63) * mm, "end": v(-22.9, -94.26) * mm});
            skLineSegment(sketch, "E86", {"start": v(26.57, -63) * mm, "end": v(24.45, -91) * mm});
            skSolve(sketch);
        }
        {
            var Q0;
            Q0=qSketchRegion(id+"F31",true);
            extrude(context, id + "F32", {"entities" : qUnion([Q0]), "operationType" : NewBodyOperationType.ADD, "depth" : 1.3 * mm, "offsetDistance" : 25 * mm});
        }
        {
            var Q0;
            Q0=makeQuery(id+"F25.opExtrude","CAP_FACE",FACE,{"disambiguationData":[OSD([sQuery(id+"F24.wireOp",EDGE,"E55.0"),sQuery(id+"F24.wireOp",EDGE,"E55.1"),sQuery(id+"F24.wireOp",EDGE,"E55.2"),sQuery(id+"F24.wireOp",EDGE,"E55.3"),sQuery(id+"F24.wireOp",EDGE,"E55.4"),sQuery(id+"F24.wireOp",EDGE,"E55.5"),sQuery(id+"F24.wireOp",EDGE,"E56.0"),sQuery(id+"F24.wireOp",EDGE,"E57.0"),sQuery(id+"F24.wireOp",EDGE,"E58.0"),sQuery(id+"F24.wireOp",EDGE,"E59.0"),sQuery(id+"F24.wireOp",EDGE,"E60.0"),sQuery(id+"F24.wireOp",EDGE,"E61.0"),sQuery(id+"F24.wireOp",EDGE,"E62.0"),sQuery(id+"F24.wireOp",EDGE,"E63.0"),sQuery(id+"F24.wireOp",EDGE,"E64.0"),sQuery(id+"F24.wireOp",EDGE,"E65.0"),sQuery(id+"F24.wireOp",EDGE,"E66.0"),sQuery(id+"F24.wireOp",EDGE,"E67.0"),sQuery(id+"F24.wireOp",EDGE,"E68.0"),sQuery(id+"F24.wireOp",EDGE,"E69.0")])],"isStart":false});
            var sketch = newSketch(context, id + "F33", { "sketchPlane" : qUnion([Q0])});
            skLineSegment(sketch, "E87.0", {"start": v(-43.5, -63.5) * mm, "end": v(-32.8, -86.78) * mm});
            skLineSegment(sketch, "E87.1", {"start": v(-32.8, -86.78) * mm, "end": v(-22.74, -93.76) * mm});
            skLineSegment(sketch, "E87.2", {"start": v(-43.5, -63.5) * mm, "end": v(36, -63.5) * mm});
            skLineSegment(sketch, "E87.3", {"start": v(-22.74, -93.76) * mm, "end": v(16.6, -93.76) * mm});
            skArc(sketch, "E87.4", {"start": v(27.34, -86.84) * mm, "mid": v(32.97, -75.66) * mm, "end": v(36, -63.5) * mm});
            skArc(sketch, "E87.5", {"start": v(24.26, -90.5) * mm, "mid": v(25.9, -88.77) * mm, "end": v(27.34, -86.84) * mm});
            skLineSegment(sketch, "E87.6", {"start": v(16.6, -90.5) * mm, "end": v(24.26, -90.5) * mm});
            skLineSegment(sketch, "E87.7", {"start": v(16.6, -93.76) * mm, "end": v(16.6, -90.5) * mm});
            skSolve(sketch);
        }
        {
            var Q0;
            Q0=qSketchRegion(id+"F33",true);
            var Q1;
            Q1=makeQuery(id+"F32.opExtrude","CAP_FACE",FACE,{"disambiguationData":[OSD([sQuery(id+"F31.wireOp",EDGE,"E74.0"),sQuery(id+"F31.wireOp",EDGE,"E75"),sQuery(id+"F31.wireOp",EDGE,"EqfmIO8x-eZOM-xre8-AD1a-nbBecVC82i3M")])],"isStart":false});
            extrude(context, id + "F34", {"entities" : qUnion([Q0]), "endBound" : BoundingType.UP_TO_SURFACE, "oppositeDirection" : true, "depth" : 25 * mm, "endBoundEntityFace" : qUnion([Q1]), "offsetDistance" : 25 * mm});
        }
        {
            var Q0;
            Q0=makeQuery(id+"F34.opExtrude","CAP_FACE",FACE,{"disambiguationData":[OSD([sQuery(id+"F33.wireOp",EDGE,"E87.0"),sQuery(id+"F33.wireOp",EDGE,"E87.1"),sQuery(id+"F33.wireOp",EDGE,"E87.2"),sQuery(id+"F33.wireOp",EDGE,"E87.3"),sQuery(id+"F33.wireOp",EDGE,"E87.4"),sQuery(id+"F33.wireOp",EDGE,"E87.5"),sQuery(id+"F33.wireOp",EDGE,"E87.6"),sQuery(id+"F33.wireOp",EDGE,"E87.7")])],"isStart":true});
            var sketch = newSketch(context, id + "F35", { "sketchPlane" : qUnion([Q0])});
            skCircle(sketch, "E88", {"center": v(32.5, -65.7) * mm, "radius": 1.4 * mm});
            skCircle(sketch, "E89", {"center": v(-40, -65.7) * mm, "radius": 1.4 * mm});
            skCircle(sketch, "E90", {"center": v(-32.8, -81.28) * mm, "radius": 1.4 * mm});
            skCircle(sketch, "E91", {"center": v(27.94, -81.28) * mm, "radius": 1.4 * mm});
            skSolve(sketch);
        }
        {
            var Q0;
            Q0=qSketchRegion(id+"F35",true);
            extrude(context, id + "F36", {"entities" : qUnion([Q0]), "operationType" : NewBodyOperationType.REMOVE, "oppositeDirection" : true, "depth" : 5 * mm, "offsetDistance" : 25 * mm});
        }
        {
            var Q0;
            {var subQ0=sQuery(id+"F16.wireOp",EDGE,"E35.bottom");var subQ1=sQuery(id+"F8.wireOp",EDGE,"E24.filletArc");var subQ2=sQuery(id+"F8.wireOp",EDGE,"E23.filletArc");var subQ3=sQuery(id+"F8.wireOp",EDGE,"E20.0");var subQ4=sQuery(id+"F8.wireOp",EDGE,"E15");var subQ5=sQuery(id+"F8.wireOp",EDGE,"E14.MirrorCS");var subQ6=sQuery(id+"F8.wireOp",EDGE,"E12");var subQ7=sQuery(id+"F2.wireOp",EDGE,"E7.right");var subQ8=sQuery(id+"F2.wireOp",EDGE,"E7.left");var subQ9=sQuery(id+"F2.wireOp",EDGE,"E7.top");var subQ10=sQuery(id+"F2.wireOp",EDGE,"E7.bottom");Q0=makeQuery(id+"F23.boolean.opBoolean","MERGE",FACE,{"derivedFrom":[makeQuery(id+"F21.boolean.opBoolean","MERGE",FACE,{"derivedFrom":[makeQuery(id+"F17.boolean.opBoolean","MERGE",FACE,{"derivedFrom":[makeQuery(id+"F5.boolean.opBoolean","MERGE",FACE,{"derivedFrom":[makeQuery(id+"F3.opExtrude","CAP_FACE",FACE,{"disambiguationData":[OSD([subQ10,subQ9,subQ8,subQ7])],"isStart":false}),makeQuery(id+"F5.opExtrude","CAP_FACE",FACE,{"disambiguationData":[OSD([subQ10,subQ9,subQ8,subQ7])],"isStart":false})]}),makeQuery(id+"F9.boolean.opBoolean","COPY",FACE,{"derivedFrom":makeQuery(id+"F9.opExtrude","CAP_FACE",FACE,{"disambiguationData":[OSD([subQ6,subQ5,subQ4,subQ3,subQ2,subQ1])],"isStart":false})}),makeQuery(id+"F17.opExtrude","SWEPT_FACE",FACE,{"disambiguationData":[OSD([subQ0])]})]}),makeQuery(id+"F21.opExtrude","CAP_FACE",FACE,{"disambiguationData":[OSD([subQ10,subQ9,subQ8,subQ7,subQ6,subQ5,subQ4,subQ3,subQ2,subQ1,subQ0])],"isStart":false})]}),makeQuery(id+"F23.opExtrude","CAP_FACE",FACE,{"disambiguationData":[OSD([subQ10,subQ9,subQ8,subQ7,subQ6,subQ5,subQ4,subQ3,subQ2,subQ1,subQ0])],"isStart":false})]});}
            var sketch = newSketch(context, id + "F37", { "sketchPlane" : qUnion([Q0])});
            skLineSegment(sketch, "E92.bottom", {"start": v(36, 36) * mm, "end": v(-36, 36) * mm});
            skLineSegment(sketch, "E92.top", {"start": v(36, 56) * mm, "end": v(-36, 56) * mm});
            skLineSegment(sketch, "E92.left", {"start": v(36, 36) * mm, "end": v(36, 56) * mm});
            skLineSegment(sketch, "E92.right", {"start": v(-36, 36) * mm, "end": v(-36, 56) * mm});
            skLineSegment(sketch, "E93.bottom", {"start": v(15, -56) * mm, "end": v(-15, -56) * mm});
            skLineSegment(sketch, "E93.top", {"start": v(15, 6) * mm, "end": v(-15, 6) * mm});
            skLineSegment(sketch, "E93.left", {"start": v(15, -56) * mm, "end": v(15, 6) * mm});
            skLineSegment(sketch, "E93.right", {"start": v(-15, -56) * mm, "end": v(-15, 6) * mm});
            skPoint(sketch, "E94", {"position": v(0, 6) * mm});
            skSolve(sketch);
        }
        {
            var Q0;
            Q0=qSketchRegion(id+"F37",true);
            extrude(context, id + "F38", {"entities" : qUnion([Q0]), "operationType" : NewBodyOperationType.REMOVE, "depth" : 25 * mm, "offsetDistance" : 25 * mm});
        }
    });
